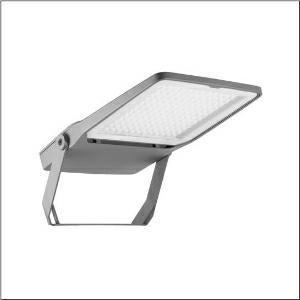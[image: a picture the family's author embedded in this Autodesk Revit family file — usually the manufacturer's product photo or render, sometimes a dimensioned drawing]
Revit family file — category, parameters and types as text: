
# Revit family: floodlight_fl_20_midi___pl43_5xa7682e2a1ac_c4a2
name_source: partatom
category: Lighting Fixtures
units: mm (PartAtom-declared; Revit-internal decimal feet)

## family parameters
Cut with Voids When Loaded = No
Host = Face
Light Source = No
Part Type = Normal
Room Calculation Point = No
Round Connector Dimension = Use Diameter
Shared = No

## types (1)
- --- (1 x LED 4000K / CRI = 70 (unbekannt), 28460 lm, 4000K)
    Apparent Load = 208 VA
    CIE Flux Codes = 32 74 99 100 100
    Color Rendering = 70
    Color Temperature = 4000K
    Default Elevation = 1800 mm
    Description = Floodlight FL 20 midi, floodlight, primary light control with lens, of plastic, primary optical cover: protective disc, of toughened safety glass, transparent, light distribution: PL43, light emission: direct distribution, primary light characteristic: asymmetric, installation type: surface-mounted, LED High Power LED, rated luminous flux: 28.460 lm, light colour: 740, colour temperature: 4000K, control gear: ECG Plus, control: overheat protection, power reduction, digital communication interface, flexible luminous flux parameterisation, time-dependent luminous flux control, electronic power reduction, with terminal, 5-pole, max. 2.5mm², mains connection: 220..240V, AC, 50/60Hz, rated input power: 208W, LED unit, of diecast aluminium, powder-coated, Siteco® metallic grey (DB 702S), length: 654 mm, width: 450 mm, height: 76mm, housing frame, of diecast aluminium, powder-coated, Siteco® metallic grey (DB 702S), mounting bracket, of steel, powder-coated, Siteco® metallic grey (DB 702S), DALIprotection rating (complete): IP66, insulation class (complete): insulation class II (safety insulation), certification: CE, ENEC, VDE, protection symbol: D, permissible ambient temperature for indoor applications: -40..+40°C, permissible ambient temperature for outdoor applications: -40..+50°C, standard: DIN EN 12944, packaging unit: 1 piece

Light Distribution: PL43
    Height = 76 mm
    Lamp = 1 x LED 4000K / CRI >= 70 (unbekannt)
    Lamp Light Flux = 28460 lm
    Lamp count = 1
    Length = 672 mm
    Luminous efficacy = 137 lm/W
    Manufacturer = Siteco
    ModVariant = No
    Model = 5XA7682E2A1AC
    Number of Poles = 1
    OnlyDefault = Yes
    Power Factor = 1
    Product Name = Floodlight FL 20 midi | PL43
    Product group = floodlight | pylon top
    ProductGroupID = 6101
    Protection Class = Protection class II
    Protection Degree = IP 66
    RLX_Detail_Level = 1
    RlxData = <blob elided: 97365 chars, md5=ab858f5a>
    Socket = socket
    Standby Power = 0 W
    System Light Flux = 28460 lm
    System Power = 208 W
    Type Comments = factory setting: luminous flux: 100 % | dim-lin: 254 | 484 mA
    Type Image = l_1005943.jpg
    URL = http://relux.com
    VarID = @adj_143693
    Voltage = 0 V
    Weight = 0.00 kg
    Width = 450 mm

## geometry (parser evidence)
native form markers: Blend x4, Sweep x11
no freeform markers — native parametric forms only
